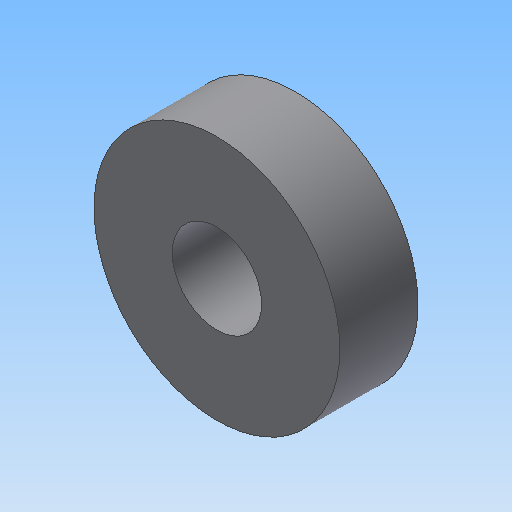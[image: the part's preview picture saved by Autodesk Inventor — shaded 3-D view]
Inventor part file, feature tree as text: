
AUTODESK INVENTOR PART (.ipt)
format: ipt  version: 2017 (Build 210142000, 142)  size: 91,136 bytes
history: native  units: in
note: dims shown in document units (in); Inventor stores cm internally (conversion verified against a paired STEP export)
features: extrude x1, sketch x1
ambient origin geometry x8: Origin, YZ Plane, XZ Plane, XY Plane, X Axis, Y Axis, Z Axis, Center Point
bodies: Solid1 (feature_tree)
feature tree (2):
  extrude  "Extrusion1"  Depth=0.2756in
  sketch  "Sketch1"  dims[d0=0.315in d1=0.8661in d2=0.2756in d3=0.0in]
